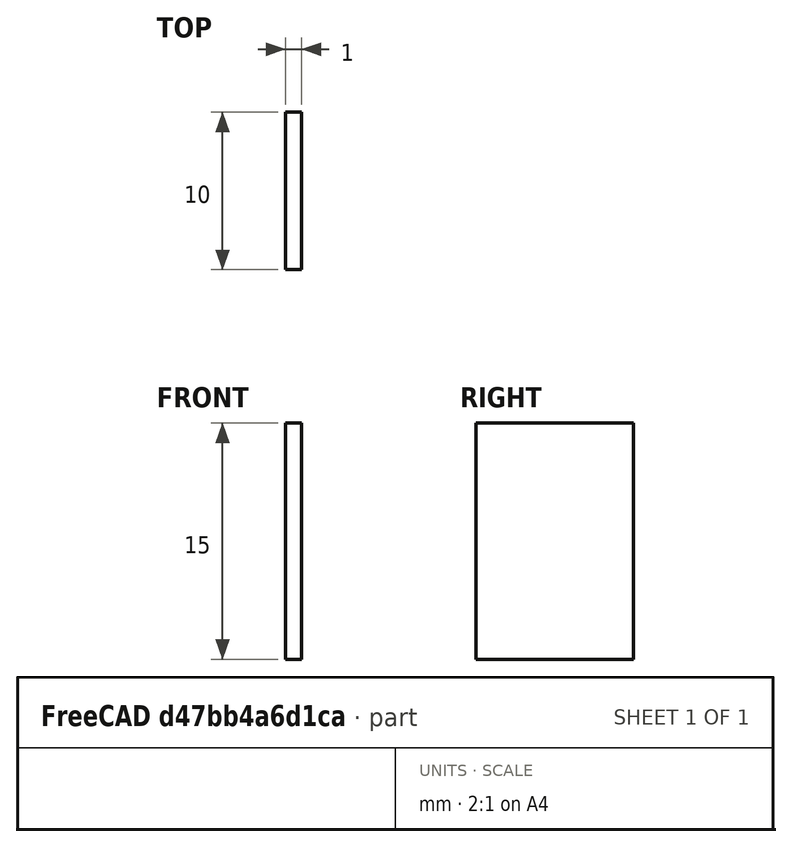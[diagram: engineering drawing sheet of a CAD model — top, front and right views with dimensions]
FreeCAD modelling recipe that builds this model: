
FCSTD DOCUMENT  (FreeCAD 0.15R4671 (Git))
Label: flexural_stage_2
License: All rights reserved
LicenseURL: http://en.wikipedia.org/wiki/All_rights_reserved
objects: Sketcher::SketchObject×1, PartDesign::Pad×1
note: 3 computed .brp shape members not serialized (recipe doc carries the construction recipe); baked Part::Feature solids carry a one-line shape summary decoded from their .brp

FEATURE [Sketcher::SketchObject] Sketch
  sketch-geometry (4):
    g0: LineSegment StartX=-0.5 StartY=5 StartZ=0 EndX=0.5 EndY=5 EndZ=0
    g1: LineSegment StartX=0.5 StartY=5 StartZ=0 EndX=0.5 EndY=-5 EndZ=0
    g2: LineSegment StartX=0.5 StartY=-5 StartZ=0 EndX=-0.5 EndY=-5 EndZ=0
    g3: LineSegment StartX=-0.5 StartY=-5 StartZ=0 EndX=-0.5 EndY=5 EndZ=0
  constraints (8):
    c: Coincident(g0,g1)
    c: Coincident(g1,g2)
    c: Coincident(g2,g3)
    c: Coincident(g3,g0)
    c: Horizontal(g0)
    c: Horizontal(g2)
    c: Vertical(g1)
    c: Vertical(g3)
FEATURE [PartDesign::Pad] Pad
  Length = 15
  Length2 = 100
  Sketch = -> Sketch
  Type = 0
